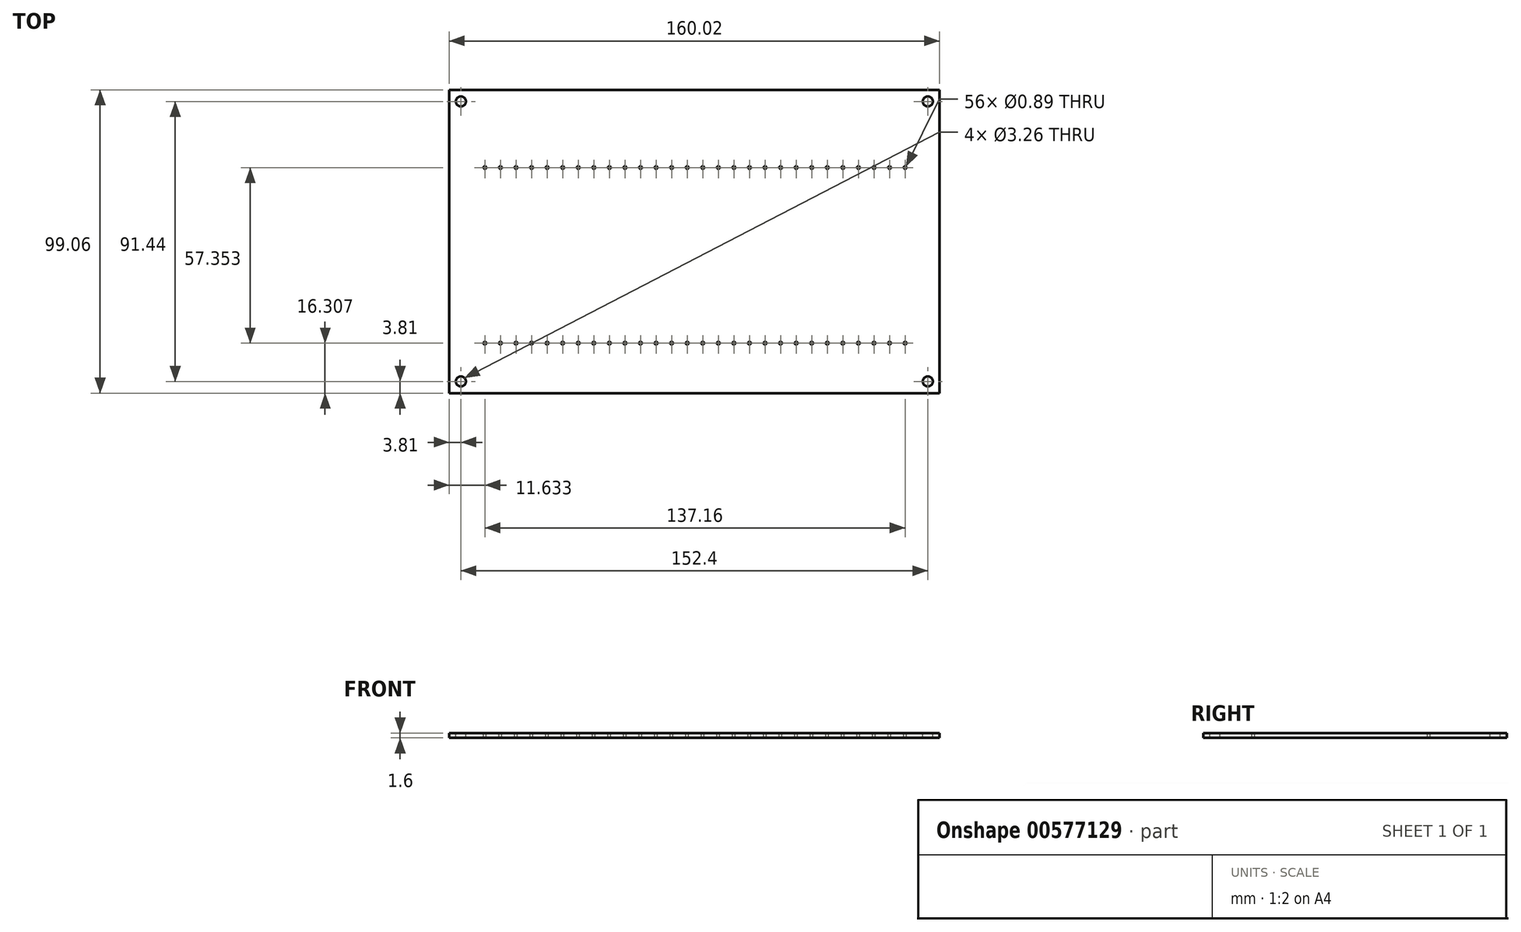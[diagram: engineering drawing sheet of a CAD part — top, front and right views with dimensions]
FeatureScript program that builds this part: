
annotation { "Feature Type Name" : "Feature", "Feature Type Description" : "" }
export const myFeature = defineFeature(function(context is Context, id is Id, definition is map)
    precondition{}
    {
        {
            var Q0;
            Q0=qCreatedBy(makeId("Top.planeOp"),FACE);
            var sketch = newSketch(context, id + "F0", { "sketchPlane" : qUnion([Q0])});
            skLineSegment(sketch, "E0.bottom", {"start": v(0, 0) * mm, "end": v(160.02, 0) * mm});
            skLineSegment(sketch, "E0.top", {"start": v(0, 99.06) * mm, "end": v(160.02, 99.06) * mm});
            skLineSegment(sketch, "E0.left", {"start": v(0, 0) * mm, "end": v(0, 99.06) * mm});
            skLineSegment(sketch, "E0.right", {"start": v(160.02, 0) * mm, "end": v(160.02, 99.06) * mm});
            skSolve(sketch);
        }
        {
            var Q0;
            Q0=qSketchRegion(id+"F0",true);
            extrude(context, id + "F1", {"entities" : qUnion([Q0]), "depth" : 1.6 * mm});
        }
        {
            var Q0;
            Q0=makeQuery(id+"F1.opExtrude","CAP_FACE",FACE,{"disambiguationData":[OSD([sQuery(id+"F0.wireOp",EDGE,"E0.bottom"),sQuery(id+"F0.wireOp",EDGE,"E0.top"),sQuery(id+"F0.wireOp",EDGE,"E0.left"),sQuery(id+"F0.wireOp",EDGE,"E0.right")])],"isStart":false});
            var sketch = newSketch(context, id + "F2", { "sketchPlane" : qUnion([Q0])});
            skPoint(sketch, "E1", {"position": v(3.81, 3.81) * mm});
            skPoint(sketch, "E2", {"position": v(3.81, 95.25) * mm});
            skPoint(sketch, "E3", {"position": v(156.21, 95.25) * mm});
            skPoint(sketch, "E4", {"position": v(156.21, 3.81) * mm});
            skSolve(sketch);
        }
        {
            var Q0;
            Q0=sQuery(id+"F2.wireOp",VERTEX,"E2");
            var Q1;
            Q1=sQuery(id+"F2.wireOp",VERTEX,"E1");
            var Q2;
            Q2=sQuery(id+"F2.wireOp",VERTEX,"E4");
            var Q3;
            Q3=sQuery(id+"F2.wireOp",VERTEX,"E3");
            var Q4;
            Q4=makeQuery(id+"F1.opExtrude","SWEPT_BODY",BODY,{"disambiguationData":[OSD([sQuery(id+"F0.wireOp",EDGE,"E0.bottom"),sQuery(id+"F0.wireOp",EDGE,"E0.top"),sQuery(id+"F0.wireOp",EDGE,"E0.left"),sQuery(id+"F0.wireOp",EDGE,"E0.right")])]});
            hole(context, id + "F3", {"style" : HoleStyle.SIMPLE, "endStyle" : HoleEndStyle.THROUGH, "standardTappedOrClearance" : lookupTablePath({ "standard" : "ANSI", "fit" : "Normal (ASME)", "size" : "#4", "type" : "Clearance" }), "standardBlindInLast" : lookupTablePath({ "fit" : "Free", "standard" : "ANSI", "size" : "#4", "type" : "Clearance" }), "holeDiameter" : 3.26 * mm, "tappedDepth" : 2.77 * mm, "tapClearance" : 3, "startFromSketch" : true, "locations" : qUnion([Q0, Q1, Q2, Q3]), "scope" : qUnion([Q4])});
        }
        {
            var Q0;
            Q0=makeQuery(id+"F1.opExtrude","CAP_FACE",FACE,{"disambiguationData":[OSD([sQuery(id+"F0.wireOp",EDGE,"E0.bottom"),sQuery(id+"F0.wireOp",EDGE,"E0.top"),sQuery(id+"F0.wireOp",EDGE,"E0.left"),sQuery(id+"F0.wireOp",EDGE,"E0.right")])],"isStart":false});
            var sketch = newSketch(context, id + "F4", { "sketchPlane" : qUnion([Q0])});
            skPoint(sketch, "E5", {"position": v(11.63, 73.66) * mm});
            skPoint(sketch, "E6.1.0.0", {"position": v(16.71, 73.66) * mm});
            skPoint(sketch, "E6.2.0.0", {"position": v(21.8, 73.66) * mm});
            skPoint(sketch, "E6.3.0.0", {"position": v(26.87, 73.66) * mm});
            skPoint(sketch, "E6.4.0.0", {"position": v(31.95, 73.66) * mm});
            skPoint(sketch, "E6.5.0.0", {"position": v(37.03, 73.66) * mm});
            skPoint(sketch, "E6.6.0.0", {"position": v(42.11, 73.66) * mm});
            skPoint(sketch, "E6.7.0.0", {"position": v(47.2, 73.66) * mm});
            skPoint(sketch, "E6.8.0.0", {"position": v(52.27, 73.66) * mm});
            skPoint(sketch, "E6.9.0.0", {"position": v(57.35, 73.66) * mm});
            skPoint(sketch, "E6.10.0.0", {"position": v(62.43, 73.66) * mm});
            skPoint(sketch, "E6.11.0.0", {"position": v(67.51, 73.66) * mm});
            skPoint(sketch, "E6.12.0.0", {"position": v(72.6, 73.66) * mm});
            skPoint(sketch, "E6.13.0.0", {"position": v(77.67, 73.66) * mm});
            skPoint(sketch, "E6.14.0.0", {"position": v(82.75, 73.66) * mm});
            skPoint(sketch, "E6.15.0.0", {"position": v(87.83, 73.66) * mm});
            skPoint(sketch, "E6.16.0.0", {"position": v(92.91, 73.66) * mm});
            skPoint(sketch, "E6.17.0.0", {"position": v(98, 73.66) * mm});
            skPoint(sketch, "E6.18.0.0", {"position": v(103.07, 73.66) * mm});
            skPoint(sketch, "E6.19.0.0", {"position": v(108.15, 73.66) * mm});
            skPoint(sketch, "E6.20.0.0", {"position": v(113.23, 73.66) * mm});
            skPoint(sketch, "E6.21.0.0", {"position": v(118.31, 73.66) * mm});
            skPoint(sketch, "E6.22.0.0", {"position": v(123.4, 73.66) * mm});
            skPoint(sketch, "E6.23.0.0", {"position": v(128.47, 73.66) * mm});
            skPoint(sketch, "E6.24.0.0", {"position": v(133.55, 73.66) * mm});
            skPoint(sketch, "E6.25.0.0", {"position": v(138.63, 73.66) * mm});
            skPoint(sketch, "E6.26.0.0", {"position": v(143.71, 73.66) * mm});
            skPoint(sketch, "E6.27.0.0", {"position": v(148.8, 73.66) * mm});
            skLineSegment(sketch, "E6.direction1", {"start": v(11.63, 73.66) * mm, "end": v(16.71, 73.66) * mm, "construction": true});
            skSolve(sketch);
        }
        {
            var Q0;
            Q0=makeQuery(id+"F4.imprint","IMPRINT",FACE,{"disambiguationData":[TD([[makeQuery(id+"F4.imprint","IMPRINT",EDGE,{"derivedFrom":makeQuery(id+"F1.opExtrude","CAP_EDGE",EDGE,{"disambiguationData":[OSD([sQuery(id+"F0.wireOp",EDGE,"E0.bottom")])],"isStart":false})}),1.0]])]});
            var sketch = newSketch(context, id + "F5", { "sketchPlane" : qUnion([Q0])});
            skPoint(sketch, "E7", {"position": v(11.63, 16.3) * mm});
            skPoint(sketch, "E8.1.0.0", {"position": v(16.71, 16.3) * mm});
            skPoint(sketch, "E8.2.0.0", {"position": v(21.8, 16.3) * mm});
            skPoint(sketch, "E8.3.0.0", {"position": v(26.87, 16.3) * mm});
            skPoint(sketch, "E8.4.0.0", {"position": v(31.95, 16.3) * mm});
            skPoint(sketch, "E8.5.0.0", {"position": v(37.03, 16.3) * mm});
            skPoint(sketch, "E8.6.0.0", {"position": v(42.11, 16.3) * mm});
            skPoint(sketch, "E8.7.0.0", {"position": v(47.2, 16.3) * mm});
            skPoint(sketch, "E8.8.0.0", {"position": v(52.27, 16.3) * mm});
            skPoint(sketch, "E8.9.0.0", {"position": v(57.35, 16.3) * mm});
            skPoint(sketch, "E8.10.0.0", {"position": v(62.43, 16.3) * mm});
            skPoint(sketch, "E8.11.0.0", {"position": v(67.51, 16.3) * mm});
            skPoint(sketch, "E8.12.0.0", {"position": v(72.6, 16.3) * mm});
            skPoint(sketch, "E8.13.0.0", {"position": v(77.67, 16.3) * mm});
            skPoint(sketch, "E8.14.0.0", {"position": v(82.75, 16.3) * mm});
            skPoint(sketch, "E8.15.0.0", {"position": v(87.83, 16.3) * mm});
            skPoint(sketch, "E8.16.0.0", {"position": v(92.91, 16.3) * mm});
            skPoint(sketch, "E8.17.0.0", {"position": v(98, 16.3) * mm});
            skPoint(sketch, "E8.18.0.0", {"position": v(103.07, 16.3) * mm});
            skPoint(sketch, "E8.19.0.0", {"position": v(108.15, 16.3) * mm});
            skPoint(sketch, "E8.20.0.0", {"position": v(113.23, 16.3) * mm});
            skPoint(sketch, "E8.21.0.0", {"position": v(118.31, 16.3) * mm});
            skPoint(sketch, "E8.22.0.0", {"position": v(123.4, 16.3) * mm});
            skPoint(sketch, "E8.23.0.0", {"position": v(128.47, 16.3) * mm});
            skPoint(sketch, "E8.24.0.0", {"position": v(133.55, 16.3) * mm});
            skPoint(sketch, "E8.25.0.0", {"position": v(138.63, 16.3) * mm});
            skPoint(sketch, "E8.26.0.0", {"position": v(143.71, 16.3) * mm});
            skPoint(sketch, "E8.27.0.0", {"position": v(148.8, 16.3) * mm});
            skLineSegment(sketch, "E8.direction1", {"start": v(11.63, 16.3) * mm, "end": v(16.71, 16.3) * mm, "construction": true});
            skSolve(sketch);
        }
        {
            var Q0;
            Q0=sQuery(id+"F4.wireOp",VERTEX,"E6.15.0.0");
            var Q1;
            Q1=sQuery(id+"F4.wireOp",VERTEX,"E6.19.0.0");
            var Q2;
            Q2=sQuery(id+"F4.wireOp",VERTEX,"E6.22.0.0");
            var Q3;
            Q3=sQuery(id+"F4.wireOp",VERTEX,"E6.26.0.0");
            var Q4;
            Q4=sQuery(id+"F4.wireOp",VERTEX,"E6.14.0.0");
            var Q5;
            Q5=sQuery(id+"F4.wireOp",VERTEX,"E6.27.0.0");
            var Q6;
            Q6=sQuery(id+"F4.wireOp",VERTEX,"E6.18.0.0");
            var Q7;
            Q7=sQuery(id+"F4.wireOp",VERTEX,"E6.21.0.0");
            var Q8;
            Q8=sQuery(id+"F4.wireOp",VERTEX,"E6.25.0.0");
            var Q9;
            Q9=sQuery(id+"F4.wireOp",VERTEX,"E6.17.0.0");
            var Q10;
            Q10=sQuery(id+"F4.wireOp",VERTEX,"E6.24.0.0");
            var Q11;
            Q11=sQuery(id+"F4.wireOp",VERTEX,"E6.10.0.0");
            var Q12;
            Q12=sQuery(id+"F4.wireOp",VERTEX,"E6.9.0.0");
            var Q13;
            Q13=sQuery(id+"F4.wireOp",VERTEX,"E6.8.0.0");
            var Q14;
            Q14=sQuery(id+"F4.wireOp",VERTEX,"E6.7.0.0");
            var Q15;
            Q15=sQuery(id+"F4.wireOp",VERTEX,"E6.6.0.0");
            var Q16;
            Q16=sQuery(id+"F4.wireOp",VERTEX,"E6.5.0.0");
            var Q17;
            Q17=sQuery(id+"F4.wireOp",VERTEX,"E6.4.0.0");
            var Q18;
            Q18=sQuery(id+"F4.wireOp",VERTEX,"E6.3.0.0");
            var Q19;
            Q19=sQuery(id+"F4.wireOp",VERTEX,"E6.2.0.0");
            var Q20;
            Q20=sQuery(id+"F4.wireOp",VERTEX,"E6.1.0.0");
            var Q21;
            Q21=sQuery(id+"F4.wireOp",VERTEX,"E5");
            var Q22;
            Q22=sQuery(id+"F4.wireOp",VERTEX,"E6.13.0.0");
            var Q23;
            Q23=sQuery(id+"F4.wireOp",VERTEX,"E6.12.0.0");
            var Q24;
            Q24=sQuery(id+"F4.wireOp",VERTEX,"E6.11.0.0");
            var Q25;
            Q25=sQuery(id+"F4.wireOp",VERTEX,"E6.16.0.0");
            var Q26;
            Q26=sQuery(id+"F4.wireOp",VERTEX,"E6.20.0.0");
            var Q27;
            Q27=sQuery(id+"F4.wireOp",VERTEX,"E6.23.0.0");
            var Q28;
            Q28=sQuery(id+"F5.wireOp",VERTEX,"E8.20.0.0");
            var Q29;
            Q29=sQuery(id+"F5.wireOp",VERTEX,"E8.2.0.0");
            var Q30;
            Q30=sQuery(id+"F5.wireOp",VERTEX,"E8.22.0.0");
            var Q31;
            Q31=sQuery(id+"F5.wireOp",VERTEX,"E8.4.0.0");
            var Q32;
            Q32=sQuery(id+"F5.wireOp",VERTEX,"E8.3.0.0");
            var Q33;
            Q33=sQuery(id+"F5.wireOp",VERTEX,"E8.8.0.0");
            var Q34;
            Q34=sQuery(id+"F5.wireOp",VERTEX,"E8.1.0.0");
            var Q35;
            Q35=sQuery(id+"F5.wireOp",VERTEX,"E8.21.0.0");
            var Q36;
            Q36=sQuery(id+"F5.wireOp",VERTEX,"E8.5.0.0");
            var Q37;
            Q37=sQuery(id+"F5.wireOp",VERTEX,"E8.17.0.0");
            var Q38;
            Q38=sQuery(id+"F5.wireOp",VERTEX,"E8.7.0.0");
            var Q39;
            Q39=sQuery(id+"F5.wireOp",VERTEX,"E8.18.0.0");
            var Q40;
            Q40=sQuery(id+"F5.wireOp",VERTEX,"E8.27.0.0");
            var Q41;
            Q41=sQuery(id+"F5.wireOp",VERTEX,"E8.6.0.0");
            var Q42;
            Q42=sQuery(id+"F5.wireOp",VERTEX,"E8.19.0.0");
            var Q43;
            Q43=sQuery(id+"F5.wireOp",VERTEX,"E8.16.0.0");
            var Q44;
            Q44=sQuery(id+"F5.wireOp",VERTEX,"E8.9.0.0");
            var Q45;
            Q45=sQuery(id+"F5.wireOp",VERTEX,"E8.15.0.0");
            var Q46;
            Q46=sQuery(id+"F5.wireOp",VERTEX,"E8.10.0.0");
            var Q47;
            Q47=sQuery(id+"F5.wireOp",VERTEX,"E8.13.0.0");
            var Q48;
            Q48=sQuery(id+"F5.wireOp",VERTEX,"E8.12.0.0");
            var Q49;
            Q49=sQuery(id+"F5.wireOp",VERTEX,"E8.11.0.0");
            var Q50;
            Q50=sQuery(id+"F5.wireOp",VERTEX,"E8.14.0.0");
            var Q51;
            Q51=sQuery(id+"F5.wireOp",VERTEX,"E8.26.0.0");
            var Q52;
            Q52=sQuery(id+"F5.wireOp",VERTEX,"E8.25.0.0");
            var Q53;
            Q53=sQuery(id+"F5.wireOp",VERTEX,"E8.24.0.0");
            var Q54;
            Q54=sQuery(id+"F5.wireOp",VERTEX,"E7");
            var Q55;
            Q55=sQuery(id+"F5.wireOp",VERTEX,"E8.23.0.0");
            var Q56;
            Q56=makeQuery(id+"F1.opExtrude","SWEPT_BODY",BODY,{"disambiguationData":[OSD([sQuery(id+"F0.wireOp",EDGE,"E0.bottom"),sQuery(id+"F0.wireOp",EDGE,"E0.top"),sQuery(id+"F0.wireOp",EDGE,"E0.left"),sQuery(id+"F0.wireOp",EDGE,"E0.right")])]});
            hole(context, id + "F6", {"style" : HoleStyle.SIMPLE, "endStyle" : HoleEndStyle.THROUGH, "holeDiameter" : 0.89 * mm, "tappedDepth" : 2.77 * mm, "tapClearance" : 3, "startFromSketch" : true, "locations" : qUnion([Q0, Q1, Q2, Q3, Q4, Q5, Q6, Q7, Q8, Q9, Q10, Q11, Q12, Q13, Q14, Q15, Q16, Q17, Q18, Q19, Q20, Q21, Q22, Q23, Q24, Q25, Q26, Q27, Q28, Q29, Q30, Q31, Q32, Q33, Q34, Q35, Q36, Q37, Q38, Q39, Q40, Q41, Q42, Q43, Q44, Q45, Q46, Q47, Q48, Q49, Q50, Q51, Q52, Q53, Q54, Q55]), "scope" : qUnion([Q56])});
        }
    });
